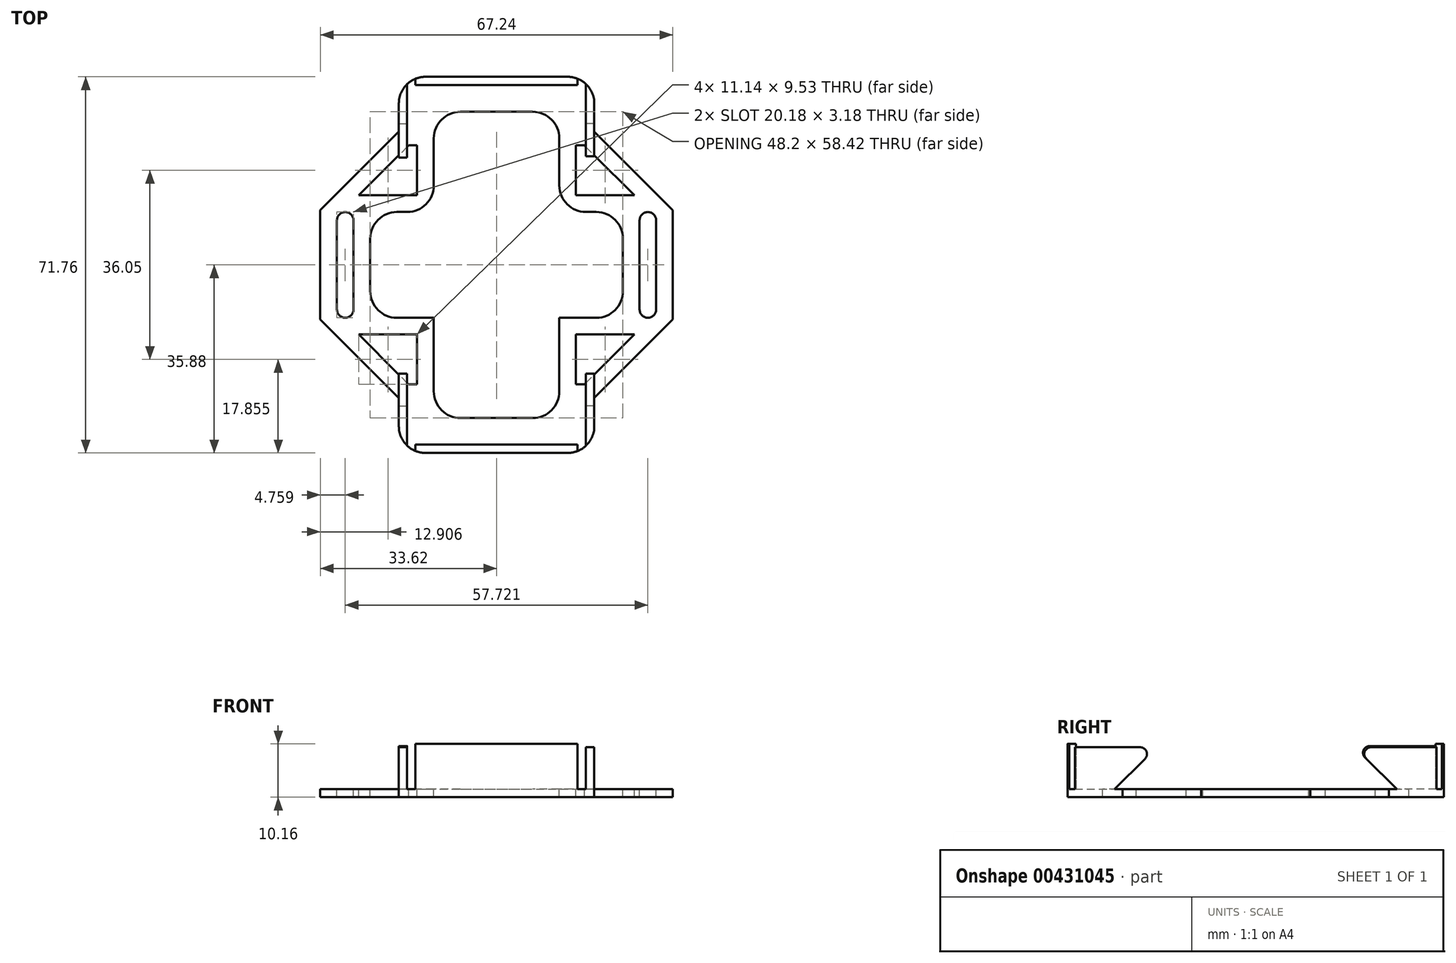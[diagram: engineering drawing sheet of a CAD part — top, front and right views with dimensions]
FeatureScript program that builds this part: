
annotation { "Feature Type Name" : "Feature", "Feature Type Description" : "" }
export const myFeature = defineFeature(function(context is Context, id is Id, definition is map)
    precondition{}
    {
        {
            var Q0;
            Q0=qCreatedBy(makeId("Front.planeOp"),FACE);
            var sketch = newSketch(context, id + "F0", { "sketchPlane" : qUnion([Q0])});
            skLineSegment(sketch, "E0", {"start": v(-17.88, 0.76) * mm, "end": v(17.88, 0.76) * mm});
            skLineSegment(sketch, "E1", {"start": v(17.88, 0.76) * mm, "end": v(18.64, 0) * mm, "construction": true});
            skLineSegment(sketch, "E2", {"start": v(18.64, 0) * mm, "end": v(18.64, -0.76) * mm});
            skLineSegment(sketch, "E3", {"start": v(18.64, -0.76) * mm, "end": v(-18.64, -0.76) * mm});
            skLineSegment(sketch, "E4", {"start": v(-18.64, -0.76) * mm, "end": v(-18.64, 0) * mm});
            skLineSegment(sketch, "E5", {"start": v(-18.64, 0) * mm, "end": v(-17.88, 0.76) * mm, "construction": true});
            skLineSegment(sketch, "E6", {"start": v(0, -0.76) * mm, "end": v(0, 0) * mm, "construction": true});
            skLineSegment(sketch, "E7", {"start": v(0, 0) * mm, "end": v(0, 0.76) * mm, "construction": true});
            skLineSegment(sketch, "E8", {"start": v(18.64, 0) * mm, "end": v(18.64, 0.76) * mm});
            skLineSegment(sketch, "E9", {"start": v(18.64, 0.76) * mm, "end": v(17.88, 0.76) * mm});
            skLineSegment(sketch, "E10", {"start": v(-18.64, 0) * mm, "end": v(-18.64, 0.76) * mm});
            skLineSegment(sketch, "E11", {"start": v(-18.64, 0.76) * mm, "end": v(-17.88, 0.76) * mm});
            skSolve(sketch);
        }
        {
            var Q0;
            Q0=makeQuery(id+"F0.imprint","IMPRINT",FACE,{"disambiguationData":[TD([[makeQuery(id+"F0.imprint","IMPRINT",EDGE,{"derivedFrom":sQuery(id+"F0.wireOp",EDGE,"E0")}),-1.0]])]});
            extrude(context, id + "F1", {"entities" : qUnion([Q0]), "endBound" : BoundingType.SYMMETRIC, "depth" : 71.75 * mm});
        }
        {
            var Q0;
            Q0=qCreatedBy(makeId("Front.planeOp"),FACE);
            var sketch = newSketch(context, id + "F2", { "sketchPlane" : qUnion([Q0])});
            skLineSegment(sketch, "E12", {"start": v(18.64, 0) * mm, "end": v(20.92, 0.76) * mm, "construction": true});
            skLineSegment(sketch, "E13", {"start": v(20.92, 0.76) * mm, "end": v(33.62, 0.76) * mm});
            skLineSegment(sketch, "E14", {"start": v(33.62, 0.76) * mm, "end": v(33.62, -0.76) * mm});
            skLineSegment(sketch, "E15", {"start": v(33.62, -0.76) * mm, "end": v(18.64, -0.76) * mm});
            skLineSegment(sketch, "E16", {"start": v(18.64, -0.76) * mm, "end": v(18.64, -0.76) * mm});
            skLineSegment(sketch, "E17", {"start": v(0, 0) * mm, "end": v(0, 24.67) * mm, "construction": true});
            skLineSegment(sketch, "E18.MirrorCS", {"start": v(-20.92, 0.76) * mm, "end": v(-33.62, 0.76) * mm});
            skLineSegment(sketch, "E19.MirrorCS", {"start": v(-33.62, 0.76) * mm, "end": v(-33.62, -0.76) * mm});
            skLineSegment(sketch, "E20.MirrorCS", {"start": v(-33.62, -0.76) * mm, "end": v(-18.64, -0.76) * mm});
            skLineSegment(sketch, "E21.MirrorCS", {"start": v(-18.64, -0.76) * mm, "end": v(-18.64, 0) * mm});
            skLineSegment(sketch, "E22.MirrorCS", {"start": v(-18.64, 0) * mm, "end": v(-20.92, 0.76) * mm, "construction": true});
            skLineSegment(sketch, "E23", {"start": v(20.92, 0.76) * mm, "end": v(18.64, 0.76) * mm});
            skLineSegment(sketch, "E24", {"start": v(18.64, 0.76) * mm, "end": v(18.64, -0.76) * mm});
            skLineSegment(sketch, "E25", {"start": v(-20.92, 0.76) * mm, "end": v(-18.64, 0.76) * mm});
            skLineSegment(sketch, "E26", {"start": v(-18.64, 0.76) * mm, "end": v(-18.64, 0) * mm});
            skSolve(sketch);
        }
        {
            var Q0;
            Q0 = qSketchRegion(id + "F2", true);
            extrude(context, id + "F3", {"entities" : qUnion([Q0]), "operationType" : NewBodyOperationType.ADD, "endBound" : BoundingType.SYMMETRIC, "depth" : 50.8 * mm});
        }
        {
            var Q0;
            Q0=makeQuery(id+"F3.boolean.opBoolean","MERGE",FACE,{"derivedFrom":[makeQuery(id+"F1.opExtrude","SWEPT_FACE",FACE,{"disambiguationData":[OSD([sQuery(id+"F0.wireOp",EDGE,"E3")])]}),makeQuery(id+"F3.opExtrude","SWEPT_FACE",FACE,{"disambiguationData":[OSD([sQuery(id+"F2.wireOp",EDGE,"E15")])]}),makeQuery(id+"F3.opExtrude","SWEPT_FACE",FACE,{"disambiguationData":[OSD([sQuery(id+"F2.wireOp",EDGE,"E20.MirrorCS")])]})]});
            var sketch = newSketch(context, id + "F4", { "sketchPlane" : qUnion([Q0])});
            skLineSegment(sketch, "E27.bottom", {"start": v(-18.64, 35.88) * mm, "end": v(-17.05, 35.88) * mm});
            skLineSegment(sketch, "E27.top", {"start": v(-18.64, 26.92) * mm, "end": v(-17.05, 26.92) * mm});
            skLineSegment(sketch, "E27.left", {"start": v(-18.64, 35.88) * mm, "end": v(-18.64, 26.92) * mm});
            skLineSegment(sketch, "E27.right", {"start": v(-17.05, 35.88) * mm, "end": v(-17.05, 26.92) * mm});
            skLineSegment(sketch, "E28", {"start": v(0, 0) * mm, "end": v(0, 50.03) * mm, "construction": true});
            skLineSegment(sketch, "E29", {"start": v(30.37, 0) * mm, "end": v(0, 0) * mm, "construction": true});
            skLineSegment(sketch, "E30.MirrorCS", {"start": v(17.05, 35.88) * mm, "end": v(17.05, 26.92) * mm});
            skLineSegment(sketch, "E31.MirrorCS", {"start": v(18.64, 35.88) * mm, "end": v(17.05, 35.88) * mm});
            skLineSegment(sketch, "E32.MirrorCS", {"start": v(18.64, 26.92) * mm, "end": v(17.05, 26.92) * mm});
            skLineSegment(sketch, "E33.MirrorCS", {"start": v(18.64, 35.88) * mm, "end": v(18.64, 26.92) * mm});
            skLineSegment(sketch, "E34.MirrorCS", {"start": v(-17.05, -35.88) * mm, "end": v(-17.05, -26.92) * mm});
            skLineSegment(sketch, "E35.MirrorCS", {"start": v(18.64, -26.92) * mm, "end": v(17.05, -26.92) * mm});
            skLineSegment(sketch, "E36.MirrorCS", {"start": v(-18.64, -35.88) * mm, "end": v(-18.64, -26.92) * mm});
            skLineSegment(sketch, "E37.MirrorCS", {"start": v(17.05, -35.88) * mm, "end": v(17.05, -26.92) * mm});
            skLineSegment(sketch, "E38.MirrorCS", {"start": v(-18.64, -26.92) * mm, "end": v(-17.05, -26.92) * mm});
            skLineSegment(sketch, "E39.MirrorCS", {"start": v(18.64, -35.88) * mm, "end": v(17.05, -35.88) * mm});
            skLineSegment(sketch, "E40.MirrorCS", {"start": v(-18.64, -35.88) * mm, "end": v(-17.05, -35.88) * mm});
            skLineSegment(sketch, "E41.MirrorCS", {"start": v(18.64, -35.88) * mm, "end": v(18.64, -26.92) * mm});
            skSolve(sketch);
        }
        {
            var Q0;
            Q0 = qSketchRegion(id + "F4", true);
            extrude(context, id + "F5", {"entities" : qUnion([Q0]), "operationType" : NewBodyOperationType.ADD, "oppositeDirection" : true, "depth" : 9.52 * mm});
        }
        {
            var Q0;
            Q0=makeQuery(id+"F1.opExtrude","SWEPT_FACE",FACE,{"disambiguationData":[OSD([sQuery(id+"F0.wireOp",EDGE,"E0")])]});
            var sketch = newSketch(context, id + "F6", { "sketchPlane" : qUnion([Q0])});
            skLineSegment(sketch, "E42.bottom", {"start": v(-15.46, 35.88) * mm, "end": v(15.46, 35.88) * mm});
            skLineSegment(sketch, "E42.top", {"start": v(-15.46, 34.3) * mm, "end": v(15.46, 34.3) * mm});
            skLineSegment(sketch, "E42.left", {"start": v(-15.46, 35.88) * mm, "end": v(-15.46, 34.3) * mm});
            skLineSegment(sketch, "E42.right", {"start": v(15.46, 35.88) * mm, "end": v(15.46, 34.3) * mm});
            skLineSegment(sketch, "E43", {"start": v(0, 0) * mm, "end": v(9.45, 0) * mm, "construction": true});
            skLineSegment(sketch, "E44.MirrorCS", {"start": v(-15.46, -35.88) * mm, "end": v(15.46, -35.88) * mm});
            skLineSegment(sketch, "E45.MirrorCS", {"start": v(-15.46, -34.3) * mm, "end": v(15.46, -34.3) * mm});
            skLineSegment(sketch, "E46.MirrorCS", {"start": v(-15.46, -35.88) * mm, "end": v(-15.46, -34.3) * mm});
            skLineSegment(sketch, "E47.MirrorCS", {"start": v(15.46, -35.88) * mm, "end": v(15.46, -34.3) * mm});
            skSolve(sketch);
        }
        {
            var Q0;
            Q0 = qSketchRegion(id + "F6", true);
            var Q1;
            Q1=makeQuery(id+"F5.opExtrude","CAP_FACE",FACE,{"disambiguationData":[OSD([sQuery(id+"F4.wireOp",EDGE,"E34.MirrorCS"),sQuery(id+"F4.wireOp",EDGE,"E36.MirrorCS"),sQuery(id+"F4.wireOp",EDGE,"E38.MirrorCS"),sQuery(id+"F4.wireOp",EDGE,"E40.MirrorCS")])],"isStart":false});
            extrude(context, id + "F7", {"entities" : qUnion([Q0, Q1]), "operationType" : NewBodyOperationType.ADD, "depth" : 8.64 * mm});
        }
        {
            var Q0;
            {var subQ0=sQuery(id+"F4.wireOp",EDGE,"E40.MirrorCS");Q0=makeQuery(id+"F7.boolean.opBoolean","MERGE",FACE,{"derivedFrom":[makeQuery(id+"F5.boolean.opBoolean","MERGE",FACE,{"derivedFrom":[makeQuery(id+"F1.opExtrude","CAP_FACE",FACE,{"disambiguationData":[OSD([sQuery(id+"F0.wireOp",EDGE,"E0"),sQuery(id+"F0.wireOp",EDGE,"E1"),sQuery(id+"F0.wireOp",EDGE,"E2"),sQuery(id+"F0.wireOp",EDGE,"E3"),sQuery(id+"F0.wireOp",EDGE,"E4"),sQuery(id+"F0.wireOp",EDGE,"E5")])],"isStart":true}),makeQuery(id+"F5.opExtrude","SWEPT_FACE",FACE,{"disambiguationData":[OSD([sQuery(id+"F4.wireOp",EDGE,"E39.MirrorCS")])]}),makeQuery(id+"F5.opExtrude","SWEPT_FACE",FACE,{"disambiguationData":[OSD([subQ0])]})]}),makeQuery(id+"F7.opExtrude","SWEPT_FACE",FACE,{"disambiguationData":[OSD([subQ0])]}),makeQuery(id+"F7.opExtrude","SWEPT_FACE",FACE,{"disambiguationData":[OSD([sQuery(id+"F6.wireOp",EDGE,"E42.bottom")])]})]});}
            var sketch = newSketch(context, id + "F8", { "sketchPlane" : qUnion([Q0])});
            skLineSegment(sketch, "E48.bottom", {"start": v(16.08, 16.65) * mm, "end": v(21.03, 16.65) * mm});
            skLineSegment(sketch, "E48.top", {"start": v(16.08, 9) * mm, "end": v(21.03, 9) * mm});
            skLineSegment(sketch, "E48.left", {"start": v(16.08, 16.65) * mm, "end": v(16.08, 9) * mm});
            skLineSegment(sketch, "E48.right", {"start": v(21.03, 16.65) * mm, "end": v(21.03, 9) * mm});
            skSolve(sketch);
        }
        {
            var Q0;
            Q0 = qSketchRegion(id + "F8", true);
            extrude(context, id + "F9", {"entities" : qUnion([Q0]), "operationType" : NewBodyOperationType.REMOVE, "endBound" : BoundingType.THROUGH_ALL, "oppositeDirection" : true, "depth" : 25.4 * mm});
        }
        {
            var Q0;
            Q0=makeQuery(id+"F3.opExtrude","SWEPT_FACE",FACE,{"disambiguationData":[OSD([sQuery(id+"F2.wireOp",EDGE,"E18.MirrorCS")])]});
            var sketch = newSketch(context, id + "F10", { "sketchPlane" : qUnion([Q0])});
            skLineSegment(sketch, "E49", {"start": v(-28.86, -8.5) * mm, "end": v(-28.86, 8.5) * mm});
            skLineSegment(sketch, "E50", {"start": v(-28.86, 8.5) * mm, "end": v(-28.86, 25.4) * mm, "construction": true});
            skLineSegment(sketch, "E51", {"start": v(-28.86, -25.4) * mm, "end": v(-28.86, -8.5) * mm, "construction": true});
            skArc(sketch, "E52.0.startCap", {"start": v(-27.27, -8.5) * mm, "mid": v(-28.86, -10.09) * mm, "end": v(-30.45, -8.5) * mm});
            skArc(sketch, "E52.0.endCap", {"start": v(-30.45, 8.5) * mm, "mid": v(-28.86, 10.09) * mm, "end": v(-27.27, 8.5) * mm});
            skLineSegment(sketch, "E52.0.left", {"start": v(-30.45, -8.5) * mm, "end": v(-30.45, 8.5) * mm});
            skLineSegment(sketch, "E52.0.right", {"start": v(-27.27, -8.5) * mm, "end": v(-27.27, 8.5) * mm});
            skLineSegment(sketch, "E53", {"start": v(0, 0) * mm, "end": v(0, 13.67) * mm, "construction": true});
            skArc(sketch, "E54.MirrorCS", {"start": v(27.27, -8.5) * mm, "mid": v(28.86, -10.09) * mm, "end": v(30.45, -8.5) * mm});
            skArc(sketch, "E55.MirrorCS", {"start": v(30.45, 8.5) * mm, "mid": v(28.86, 10.09) * mm, "end": v(27.27, 8.5) * mm});
            skLineSegment(sketch, "E56.MirrorCS", {"start": v(30.45, -8.5) * mm, "end": v(30.45, 8.5) * mm});
            skLineSegment(sketch, "E57.MirrorCS", {"start": v(27.27, -8.5) * mm, "end": v(27.27, 8.5) * mm});
            skLineSegment(sketch, "E58.bottom", {"start": v(-11.97, 29.21) * mm, "end": v(11.97, 29.21) * mm});
            skLineSegment(sketch, "E58.top", {"start": v(-11.97, -29.21) * mm, "end": v(11.97, -29.21) * mm});
            skLineSegment(sketch, "E58.left", {"start": v(-11.97, 29.21) * mm, "end": v(-11.97, -29.21) * mm});
            skLineSegment(sketch, "E58.right", {"start": v(11.97, 29.21) * mm, "end": v(11.97, -29.21) * mm});
            skSolve(sketch);
        }
        {
            var Q0;
            Q0 = qSketchRegion(id + "F10", true);
            extrude(context, id + "F11", {"entities" : qUnion([Q0]), "operationType" : NewBodyOperationType.REMOVE, "endBound" : BoundingType.THROUGH_ALL, "oppositeDirection" : true, "depth" : 25.4 * mm});
        }
        {
            var Q0;
            Q0=makeQuery(id+"F3.boolean.opBoolean","MERGE",FACE,{"derivedFrom":[makeQuery(id+"F1.opExtrude","SWEPT_FACE",FACE,{"disambiguationData":[OSD([sQuery(id+"F0.wireOp",EDGE,"E0"),sQuery(id+"F0.wireOp",EDGE,"E9"),sQuery(id+"F0.wireOp",EDGE,"E11")])]}),makeQuery(id+"F3.opExtrude","SWEPT_FACE",FACE,{"disambiguationData":[OSD([sQuery(id+"F2.wireOp",EDGE,"E13"),sQuery(id+"F2.wireOp",EDGE,"E23")])]}),makeQuery(id+"F3.opExtrude","SWEPT_FACE",FACE,{"disambiguationData":[OSD([sQuery(id+"F2.wireOp",EDGE,"E18.MirrorCS"),sQuery(id+"F2.wireOp",EDGE,"E25")])]})]});
            var sketch = newSketch(context, id + "F12", { "sketchPlane" : qUnion([Q0])});
            skLineSegment(sketch, "E59", {"start": v(18.64, 25.4) * mm, "end": v(33.62, 10.41) * mm});
            skLineSegment(sketch, "E60", {"start": v(33.62, 10.41) * mm, "end": v(33.62, 25.4) * mm});
            skLineSegment(sketch, "E61", {"start": v(33.62, 25.4) * mm, "end": v(18.64, 25.4) * mm});
            skLineSegment(sketch, "E62", {"start": v(18.64, -25.4) * mm, "end": v(33.62, -10.41) * mm});
            skLineSegment(sketch, "E63", {"start": v(33.62, -10.41) * mm, "end": v(33.62, -25.4) * mm});
            skLineSegment(sketch, "E64", {"start": v(33.62, -25.4) * mm, "end": v(18.64, -25.4) * mm});
            skLineSegment(sketch, "E65", {"start": v(-33.62, 25.4) * mm, "end": v(-18.64, 25.4) * mm});
            skLineSegment(sketch, "E66", {"start": v(-18.64, 25.4) * mm, "end": v(-33.62, 10.41) * mm});
            skLineSegment(sketch, "E67", {"start": v(-33.62, 10.41) * mm, "end": v(-33.62, 25.4) * mm});
            skLineSegment(sketch, "E68", {"start": v(-33.62, -25.4) * mm, "end": v(-18.64, -25.4) * mm});
            skLineSegment(sketch, "E69", {"start": v(-18.64, -25.4) * mm, "end": v(-33.62, -10.41) * mm});
            skLineSegment(sketch, "E70", {"start": v(-33.62, -10.41) * mm, "end": v(-33.62, -25.4) * mm});
            skSolve(sketch);
        }
        {
            var Q0;
            Q0 = qSketchRegion(id + "F12", true);
            extrude(context, id + "F13", {"entities" : qUnion([Q0]), "operationType" : NewBodyOperationType.REMOVE, "oppositeDirection" : true, "depth" : 25.4 * mm});
        }
        {
            var Q0;
            Q0=makeQuery(id+"F3.boolean.opBoolean","MERGE",FACE,{"derivedFrom":[makeQuery(id+"F1.opExtrude","SWEPT_FACE",FACE,{"disambiguationData":[OSD([sQuery(id+"F0.wireOp",EDGE,"E0"),sQuery(id+"F0.wireOp",EDGE,"E9"),sQuery(id+"F0.wireOp",EDGE,"E11")])]}),makeQuery(id+"F3.opExtrude","SWEPT_FACE",FACE,{"disambiguationData":[OSD([sQuery(id+"F2.wireOp",EDGE,"E13"),sQuery(id+"F2.wireOp",EDGE,"E23")])]}),makeQuery(id+"F3.opExtrude","SWEPT_FACE",FACE,{"disambiguationData":[OSD([sQuery(id+"F2.wireOp",EDGE,"E18.MirrorCS"),sQuery(id+"F2.wireOp",EDGE,"E25")])]})]});
            var sketch = newSketch(context, id + "F14", { "sketchPlane" : qUnion([Q0])});
            skLineSegment(sketch, "E71", {"start": v(-11.97, 10.09) * mm, "end": v(-24.1, 10.09) * mm});
            skLineSegment(sketch, "E72", {"start": v(-24.1, 10.09) * mm, "end": v(-24.1, -10.09) * mm});
            skLineSegment(sketch, "E73", {"start": v(-24.1, -10.09) * mm, "end": v(-11.97, -10.09) * mm});
            skLineSegment(sketch, "E74", {"start": v(-11.97, -10.09) * mm, "end": v(-11.97, 10.09) * mm});
            skLineSegment(sketch, "E75", {"start": v(-28.86, 10.09) * mm, "end": v(-24.1, 10.09) * mm, "construction": true});
            skLineSegment(sketch, "E76", {"start": v(-28.86, -10.09) * mm, "end": v(-24.1, -10.09) * mm, "construction": true});
            skLineSegment(sketch, "E77", {"start": v(-33.62, 0) * mm, "end": v(-30.45, 0) * mm, "construction": true});
            skLineSegment(sketch, "E78", {"start": v(-27.27, 0) * mm, "end": v(-24.1, 0) * mm, "construction": true});
            skLineSegment(sketch, "E79", {"start": v(0, 0) * mm, "end": v(0, -13.97) * mm, "construction": true});
            skLineSegment(sketch, "E80.MirrorCS", {"start": v(24.1, -10.09) * mm, "end": v(11.97, -10.09) * mm});
            skLineSegment(sketch, "E81.MirrorCS", {"start": v(11.97, -10.09) * mm, "end": v(11.97, 10.09) * mm});
            skLineSegment(sketch, "E82.MirrorCS", {"start": v(11.97, 10.09) * mm, "end": v(24.1, 10.09) * mm});
            skLineSegment(sketch, "E83.MirrorCS", {"start": v(24.1, 10.09) * mm, "end": v(24.1, -10.09) * mm});
            skLineSegment(sketch, "E84", {"start": v(-23.1, 16.44) * mm, "end": v(-26.28, 13.26) * mm});
            skLineSegment(sketch, "E85", {"start": v(-26.28, 13.26) * mm, "end": v(-15.14, 13.26) * mm});
            skLineSegment(sketch, "E86", {"start": v(-15.14, 13.26) * mm, "end": v(-15.14, 16.44) * mm});
            skLineSegment(sketch, "E87", {"start": v(-15.14, 16.44) * mm, "end": v(-23.1, 16.44) * mm});
            skLineSegment(sketch, "E88", {"start": v(-18.03, 13.26) * mm, "end": v(-18.03, 10.09) * mm, "construction": true});
            skLineSegment(sketch, "E89", {"start": v(-15.14, 16.36) * mm, "end": v(-11.97, 16.36) * mm, "construction": true});
            skLineSegment(sketch, "E90", {"start": v(-26.94, 17.1) * mm, "end": v(-24.7, 14.85) * mm, "construction": true});
            skLineSegment(sketch, "E91", {"start": v(-16.76, 19.61) * mm, "end": v(-15.14, 19.61) * mm});
            skLineSegment(sketch, "E92", {"start": v(-15.14, 19.61) * mm, "end": v(-15.14, 22.79) * mm});
            skLineSegment(sketch, "E93", {"start": v(-15.14, 22.79) * mm, "end": v(-16.76, 22.79) * mm});
            skLineSegment(sketch, "E94", {"start": v(-16.76, 22.79) * mm, "end": v(-16.76, 19.61) * mm, "construction": true});
            skLineSegment(sketch, "E95", {"start": v(-15.95, 19.61) * mm, "end": v(-15.95, 16.44) * mm, "construction": true});
            skLineSegment(sketch, "E96", {"start": v(-16.76, 22.79) * mm, "end": v(-19, 25.03) * mm, "construction": true});
            skLineSegment(sketch, "E97", {"start": v(-16.76, 22.79) * mm, "end": v(-19.93, 19.61) * mm});
            skLineSegment(sketch, "E98", {"start": v(-19.93, 19.61) * mm, "end": v(-16.76, 19.61) * mm});
            skLineSegment(sketch, "E99.MirrorCS", {"start": v(19.93, 19.61) * mm, "end": v(16.76, 19.61) * mm});
            skLineSegment(sketch, "E100.MirrorCS", {"start": v(15.14, 22.79) * mm, "end": v(16.76, 22.79) * mm});
            skLineSegment(sketch, "E101.MirrorCS", {"start": v(15.14, 16.44) * mm, "end": v(23.1, 16.44) * mm});
            skLineSegment(sketch, "E102.MirrorCS", {"start": v(23.1, 16.44) * mm, "end": v(26.28, 13.26) * mm});
            skLineSegment(sketch, "E103.MirrorCS", {"start": v(16.76, 19.61) * mm, "end": v(15.14, 19.61) * mm});
            skLineSegment(sketch, "E104.MirrorCS", {"start": v(15.14, 13.26) * mm, "end": v(15.14, 16.44) * mm});
            skLineSegment(sketch, "E105.MirrorCS", {"start": v(15.14, 19.61) * mm, "end": v(15.14, 22.79) * mm});
            skLineSegment(sketch, "E106.MirrorCS", {"start": v(16.76, 22.79) * mm, "end": v(19.93, 19.61) * mm});
            skLineSegment(sketch, "E107", {"start": v(15.14, 13.26) * mm, "end": v(26.28, 13.26) * mm});
            skLineSegment(sketch, "E108", {"start": v(0, 0) * mm, "end": v(6.74, 0) * mm, "construction": true});
            skLineSegment(sketch, "E109.MirrorCS", {"start": v(15.14, -13.26) * mm, "end": v(26.28, -13.26) * mm});
            skLineSegment(sketch, "E110.MirrorCS", {"start": v(15.14, -13.26) * mm, "end": v(15.14, -16.44) * mm});
            skLineSegment(sketch, "E111.MirrorCS", {"start": v(15.14, -16.44) * mm, "end": v(23.1, -16.44) * mm});
            skLineSegment(sketch, "E112.MirrorCS", {"start": v(23.1, -16.44) * mm, "end": v(26.28, -13.26) * mm});
            skLineSegment(sketch, "E113.MirrorCS", {"start": v(19.93, -19.61) * mm, "end": v(16.76, -19.61) * mm});
            skLineSegment(sketch, "E114.MirrorCS", {"start": v(16.76, -22.79) * mm, "end": v(19.93, -19.61) * mm});
            skLineSegment(sketch, "E115.MirrorCS", {"start": v(16.76, -19.61) * mm, "end": v(15.14, -19.61) * mm});
            skLineSegment(sketch, "E116.MirrorCS", {"start": v(15.14, -19.61) * mm, "end": v(15.14, -22.79) * mm});
            skLineSegment(sketch, "E117.MirrorCS", {"start": v(15.14, -22.79) * mm, "end": v(16.76, -22.79) * mm});
            skLineSegment(sketch, "E118.MirrorCS", {"start": v(-26.28, -13.26) * mm, "end": v(-15.14, -13.26) * mm});
            skLineSegment(sketch, "E119.MirrorCS", {"start": v(-23.1, -16.44) * mm, "end": v(-26.28, -13.26) * mm});
            skLineSegment(sketch, "E120.MirrorCS", {"start": v(-15.14, -16.44) * mm, "end": v(-23.1, -16.44) * mm});
            skLineSegment(sketch, "E121.MirrorCS", {"start": v(-15.14, -13.26) * mm, "end": v(-15.14, -16.44) * mm});
            skLineSegment(sketch, "E122.MirrorCS", {"start": v(-16.76, -19.61) * mm, "end": v(-15.14, -19.61) * mm});
            skLineSegment(sketch, "E123.MirrorCS", {"start": v(-19.93, -19.61) * mm, "end": v(-16.76, -19.61) * mm});
            skLineSegment(sketch, "E124.MirrorCS", {"start": v(-16.76, -22.79) * mm, "end": v(-19.93, -19.61) * mm});
            skLineSegment(sketch, "E125.MirrorCS", {"start": v(-15.14, -19.61) * mm, "end": v(-15.14, -22.79) * mm});
            skLineSegment(sketch, "E126.MirrorCS", {"start": v(-15.14, -22.79) * mm, "end": v(-16.76, -22.79) * mm});
            skSolve(sketch);
        }
        {
            var Q0;
            Q0 = qSketchRegion(id + "F14", true);
            extrude(context, id + "F15", {"entities" : qUnion([Q0]), "operationType" : NewBodyOperationType.REMOVE, "oppositeDirection" : true, "depth" : 25.4 * mm});
        }
        {
            var Q0;
            Q0=makeQuery(id+"F13.boolean.opBoolean","COPY",EDGE,{"derivedFrom":makeQuery(id+"F13.opExtrude","SWEPT_EDGE",EDGE,{"disambiguationData":[OSD([sQuery(id+"F2.wireOp",EDGE,"E18.MirrorCS"),sQuery(id+"F2.wireOp",EDGE,"E19.MirrorCS"),sQuery(id+"F12.wireOp",EDGE,"E69"),sQuery(id+"F12.wireOp",EDGE,"E70")])]})});
            var Q1;
            Q1=makeQuery(id+"F13.boolean.opBoolean","COPY",EDGE,{"derivedFrom":makeQuery(id+"F13.opExtrude","SWEPT_EDGE",EDGE,{"disambiguationData":[OSD([sQuery(id+"F2.wireOp",EDGE,"E18.MirrorCS"),sQuery(id+"F2.wireOp",EDGE,"E19.MirrorCS"),sQuery(id+"F12.wireOp",EDGE,"E66"),sQuery(id+"F12.wireOp",EDGE,"E67")])]})});
            var Q2;
            Q2=makeQuery(id+"F15.boolean.opBoolean","COPY",EDGE,{"derivedFrom":makeQuery(id+"F15.opExtrude","SWEPT_EDGE",EDGE,{"disambiguationData":[OSD([sQuery(id+"F14.wireOp",EDGE,"E71"),sQuery(id+"F14.wireOp",EDGE,"E72")])]})});
            var Q3;
            Q3=makeQuery(id+"F15.boolean.opBoolean","COPY",EDGE,{"derivedFrom":makeQuery(id+"F15.opExtrude","SWEPT_EDGE",EDGE,{"disambiguationData":[OSD([sQuery(id+"F14.wireOp",EDGE,"E72"),sQuery(id+"F14.wireOp",EDGE,"E73")])]})});
            var Q4;
            Q4=makeQuery(id+"F15.boolean.opBoolean","COPY",EDGE,{"derivedFrom":makeQuery(id+"F15.opExtrude","SWEPT_EDGE",EDGE,{"disambiguationData":[OSD([sQuery(id+"F10.wireOp",EDGE,"E58.left"),sQuery(id+"F14.wireOp",EDGE,"E73"),sQuery(id+"F14.wireOp",EDGE,"E74")])]})});
            var Q5;
            Q5=makeQuery(id+"F15.boolean.opBoolean","COPY",EDGE,{"derivedFrom":makeQuery(id+"F15.opExtrude","SWEPT_EDGE",EDGE,{"disambiguationData":[OSD([sQuery(id+"F10.wireOp",EDGE,"E58.left"),sQuery(id+"F14.wireOp",EDGE,"E71"),sQuery(id+"F14.wireOp",EDGE,"E74")])]})});
            var Q6;
            Q6=makeQuery(id+"F11.boolean.opBoolean","COPY",EDGE,{"derivedFrom":makeQuery(id+"F11.opExtrude","SWEPT_EDGE",EDGE,{"disambiguationData":[OSD([sQuery(id+"F10.wireOp",EDGE,"E58.bottom"),sQuery(id+"F10.wireOp",EDGE,"E58.left")])]})});
            var Q7;
            Q7=makeQuery(id+"F11.boolean.opBoolean","COPY",EDGE,{"derivedFrom":makeQuery(id+"F11.opExtrude","SWEPT_EDGE",EDGE,{"disambiguationData":[OSD([sQuery(id+"F10.wireOp",EDGE,"E58.bottom"),sQuery(id+"F10.wireOp",EDGE,"E58.right")])]})});
            var Q8;
            Q8=makeQuery(id+"F15.boolean.opBoolean","COPY",EDGE,{"derivedFrom":makeQuery(id+"F15.opExtrude","SWEPT_EDGE",EDGE,{"disambiguationData":[OSD([sQuery(id+"F10.wireOp",EDGE,"E58.right"),sQuery(id+"F14.wireOp",EDGE,"E81.MirrorCS"),sQuery(id+"F14.wireOp",EDGE,"E82.MirrorCS")])]})});
            var Q9;
            Q9=makeQuery(id+"F15.boolean.opBoolean","COPY",EDGE,{"derivedFrom":makeQuery(id+"F15.opExtrude","SWEPT_EDGE",EDGE,{"disambiguationData":[OSD([sQuery(id+"F14.wireOp",EDGE,"E82.MirrorCS"),sQuery(id+"F14.wireOp",EDGE,"E83.MirrorCS")])]})});
            var Q10;
            Q10=makeQuery(id+"F15.boolean.opBoolean","COPY",EDGE,{"derivedFrom":makeQuery(id+"F15.opExtrude","SWEPT_EDGE",EDGE,{"disambiguationData":[OSD([sQuery(id+"F14.wireOp",EDGE,"E80.MirrorCS"),sQuery(id+"F14.wireOp",EDGE,"E83.MirrorCS")])]})});
            var Q11;
            Q11=makeQuery(id+"F15.boolean.opBoolean","COPY",EDGE,{"derivedFrom":makeQuery(id+"F15.opExtrude","SWEPT_EDGE",EDGE,{"disambiguationData":[OSD([sQuery(id+"F10.wireOp",EDGE,"E58.right"),sQuery(id+"F14.wireOp",EDGE,"E80.MirrorCS"),sQuery(id+"F14.wireOp",EDGE,"E81.MirrorCS")])]})});
            var Q12;
            Q12=makeQuery(id+"F11.boolean.opBoolean","COPY",EDGE,{"derivedFrom":makeQuery(id+"F11.opExtrude","SWEPT_EDGE",EDGE,{"disambiguationData":[OSD([sQuery(id+"F10.wireOp",EDGE,"E58.top"),sQuery(id+"F10.wireOp",EDGE,"E58.right")])]})});
            var Q13;
            Q13=makeQuery(id+"F11.boolean.opBoolean","COPY",EDGE,{"derivedFrom":makeQuery(id+"F11.opExtrude","SWEPT_EDGE",EDGE,{"disambiguationData":[OSD([sQuery(id+"F10.wireOp",EDGE,"E58.top"),sQuery(id+"F10.wireOp",EDGE,"E58.left")])]})});
            var Q14;
            Q14=makeQuery(id+"F13.boolean.opBoolean","COPY",EDGE,{"derivedFrom":makeQuery(id+"F13.opExtrude","SWEPT_EDGE",EDGE,{"disambiguationData":[OSD([sQuery(id+"F2.wireOp",EDGE,"E13"),sQuery(id+"F2.wireOp",EDGE,"E14"),sQuery(id+"F12.wireOp",EDGE,"E62"),sQuery(id+"F12.wireOp",EDGE,"E63")])]})});
            var Q15;
            Q15=makeQuery(id+"F13.boolean.opBoolean","COPY",EDGE,{"derivedFrom":makeQuery(id+"F13.opExtrude","SWEPT_EDGE",EDGE,{"disambiguationData":[OSD([sQuery(id+"F2.wireOp",EDGE,"E13"),sQuery(id+"F2.wireOp",EDGE,"E14"),sQuery(id+"F12.wireOp",EDGE,"E59"),sQuery(id+"F12.wireOp",EDGE,"E60")])]})});
            var Q16;
            Q16=makeQuery(id+"F5.boolean.opBoolean","MERGE",EDGE,{"derivedFrom":[makeQuery(id+"F1.opExtrude","CAP_EDGE",EDGE,{"disambiguationData":[OSD([sQuery(id+"F0.wireOp",EDGE,"E2"),sQuery(id+"F0.wireOp",EDGE,"E8")])],"isStart":true}),makeQuery(id+"F5.opExtrude","SWEPT_EDGE",EDGE,{"disambiguationData":[OSD([sQuery(id+"F4.wireOp",EDGE,"E39.MirrorCS"),sQuery(id+"F4.wireOp",EDGE,"E41.MirrorCS")])]})]});
            var Q17;
            {var subQ0=sQuery(id+"F4.wireOp",EDGE,"E40.MirrorCS");var subQ1=sQuery(id+"F4.wireOp",EDGE,"E36.MirrorCS");Q17=makeQuery(id+"F7.boolean.opBoolean","MERGE",EDGE,{"derivedFrom":[makeQuery(id+"F5.boolean.opBoolean","MERGE",EDGE,{"derivedFrom":[makeQuery(id+"F1.opExtrude","CAP_EDGE",EDGE,{"disambiguationData":[OSD([sQuery(id+"F0.wireOp",EDGE,"E4"),sQuery(id+"F0.wireOp",EDGE,"E10")])],"isStart":true}),makeQuery(id+"F5.opExtrude","SWEPT_EDGE",EDGE,{"disambiguationData":[OSD([subQ1,subQ0])]})]}),makeQuery(id+"F7.opExtrude","SWEPT_EDGE",EDGE,{"disambiguationData":[OSD([subQ1,subQ0])]})]});}
            var Q18;
            Q18=makeQuery(id+"F5.boolean.opBoolean","MERGE",EDGE,{"derivedFrom":[makeQuery(id+"F1.opExtrude","CAP_EDGE",EDGE,{"disambiguationData":[OSD([sQuery(id+"F0.wireOp",EDGE,"E2"),sQuery(id+"F0.wireOp",EDGE,"E8")])],"isStart":false}),makeQuery(id+"F5.opExtrude","SWEPT_EDGE",EDGE,{"disambiguationData":[OSD([sQuery(id+"F4.wireOp",EDGE,"E31.MirrorCS"),sQuery(id+"F4.wireOp",EDGE,"E33.MirrorCS")])]})]});
            var Q19;
            Q19=makeQuery(id+"F5.boolean.opBoolean","MERGE",EDGE,{"derivedFrom":[makeQuery(id+"F1.opExtrude","CAP_EDGE",EDGE,{"disambiguationData":[OSD([sQuery(id+"F0.wireOp",EDGE,"E4"),sQuery(id+"F0.wireOp",EDGE,"E10")])],"isStart":false}),makeQuery(id+"F5.opExtrude","SWEPT_EDGE",EDGE,{"disambiguationData":[OSD([sQuery(id+"F4.wireOp",EDGE,"E27.bottom"),sQuery(id+"F4.wireOp",EDGE,"E27.left")])]})]});
            fillet(context, id + "F16", {"entities" : qUnion([Q0, Q1, Q2, Q3, Q4, Q5, Q6, Q7, Q8, Q9, Q10, Q11, Q12, Q13, Q14, Q15, Q16, Q17, Q18, Q19]), "radius" : 5.08 * mm, "tangentPropagation" : true, "allowEdgeOverflow" : false});
        }
        {
            var Q0;
            Q0=makeQuery(id+"F3.boolean.opBoolean","MERGE",FACE,{"derivedFrom":[makeQuery(id+"F1.opExtrude","SWEPT_FACE",FACE,{"disambiguationData":[OSD([sQuery(id+"F0.wireOp",EDGE,"E0"),sQuery(id+"F0.wireOp",EDGE,"E9"),sQuery(id+"F0.wireOp",EDGE,"E11")])]}),makeQuery(id+"F3.opExtrude","SWEPT_FACE",FACE,{"disambiguationData":[OSD([sQuery(id+"F2.wireOp",EDGE,"E13"),sQuery(id+"F2.wireOp",EDGE,"E23")])]}),makeQuery(id+"F3.opExtrude","SWEPT_FACE",FACE,{"disambiguationData":[OSD([sQuery(id+"F2.wireOp",EDGE,"E18.MirrorCS"),sQuery(id+"F2.wireOp",EDGE,"E25")])]})]});
            var sketch = newSketch(context, id + "F17", { "sketchPlane" : qUnion([Q0])});
            skLineSegment(sketch, "E127", {"start": v(-19.93, 19.61) * mm, "end": v(-23.1, 16.44) * mm});
            skLineSegment(sketch, "E128", {"start": v(-23.1, 16.44) * mm, "end": v(-15.14, 16.44) * mm});
            skLineSegment(sketch, "E129", {"start": v(-15.14, 16.44) * mm, "end": v(-15.14, 19.61) * mm});
            skLineSegment(sketch, "E130", {"start": v(-15.14, 19.61) * mm, "end": v(-19.93, 19.61) * mm});
            skLineSegment(sketch, "E131", {"start": v(15.14, 19.61) * mm, "end": v(15.14, 16.44) * mm});
            skLineSegment(sketch, "E132", {"start": v(15.14, 16.44) * mm, "end": v(23.1, 16.44) * mm});
            skLineSegment(sketch, "E133", {"start": v(23.1, 16.44) * mm, "end": v(19.93, 19.61) * mm});
            skLineSegment(sketch, "E134", {"start": v(19.93, 19.61) * mm, "end": v(15.14, 19.61) * mm});
            skLineSegment(sketch, "E135", {"start": v(15.14, -16.44) * mm, "end": v(15.14, -19.61) * mm});
            skLineSegment(sketch, "E136", {"start": v(15.14, -19.61) * mm, "end": v(19.93, -19.61) * mm});
            skLineSegment(sketch, "E137", {"start": v(19.93, -19.61) * mm, "end": v(23.1, -16.44) * mm});
            skLineSegment(sketch, "E138", {"start": v(23.1, -16.44) * mm, "end": v(15.14, -16.44) * mm});
            skLineSegment(sketch, "E139", {"start": v(-23.1, -16.44) * mm, "end": v(-19.93, -19.61) * mm});
            skLineSegment(sketch, "E140", {"start": v(-19.93, -19.61) * mm, "end": v(-15.14, -19.61) * mm});
            skLineSegment(sketch, "E141", {"start": v(-15.14, -19.61) * mm, "end": v(-15.14, -16.44) * mm});
            skLineSegment(sketch, "E142", {"start": v(-15.14, -16.44) * mm, "end": v(-23.1, -16.44) * mm});
            skSolve(sketch);
        }
        {
            var Q0;
            Q0 = qSketchRegion(id + "F17", true);
            extrude(context, id + "F18", {"entities" : qUnion([Q0]), "operationType" : NewBodyOperationType.REMOVE, "oppositeDirection" : true, "depth" : 25.4 * mm});
        }
        {
            var Q0;
            {var subQ0=sQuery(id+"F2.wireOp",EDGE,"E23");var subQ1=sQuery(id+"F2.wireOp",EDGE,"E15");var subQ2=sQuery(id+"F2.wireOp",EDGE,"E13");var subQ7=sQuery(id+"F0.wireOp",EDGE,"E8");var subQ8=sQuery(id+"F0.wireOp",EDGE,"E2");Q0=makeQuery(id+"F5.boolean.opBoolean","MERGE",FACE,{"derivedFrom":[makeQuery(id+"F3.boolean.opBoolean","SPLIT",FACE,{"disambiguationData":[TD([makeQuery(id+"F3.opExtrude","CAP_FACE",FACE,{"disambiguationData":[OSD([subQ2,sQuery(id+"F2.wireOp",EDGE,"E14"),subQ1,subQ0,sQuery(id+"F2.wireOp",EDGE,"E24")])],"isStart":true})])],"derivedFrom":makeQuery(id+"F1.opExtrude","SWEPT_FACE",FACE,{"disambiguationData":[OSD([subQ8,subQ7])]})}),makeQuery(id+"F5.opExtrude","SWEPT_FACE",FACE,{"disambiguationData":[OSD([sQuery(id+"F4.wireOp",EDGE,"E41.MirrorCS")])]})]});}
            var sketch = newSketch(context, id + "F19", { "sketchPlane" : qUnion([Q0])});
            skLineSegment(sketch, "E143", {"start": v(26.92, 0.76) * mm, "end": v(18.92, 8.76) * mm});
            skLineSegment(sketch, "E144", {"start": v(18.92, 8.76) * mm, "end": v(26.92, 8.76) * mm});
            skLineSegment(sketch, "E145", {"start": v(26.92, 8.76) * mm, "end": v(26.92, 0.76) * mm});
            skLineSegment(sketch, "E146", {"start": v(0, 0) * mm, "end": v(0, 31.58) * mm, "construction": true});
            skLineSegment(sketch, "E147.MirrorCS", {"start": v(-26.92, 0.76) * mm, "end": v(-18.92, 8.76) * mm});
            skLineSegment(sketch, "E148.MirrorCS", {"start": v(-18.92, 8.76) * mm, "end": v(-26.92, 8.76) * mm});
            skLineSegment(sketch, "E149.MirrorCS", {"start": v(-26.92, 8.76) * mm, "end": v(-26.92, 0.76) * mm});
            skSolve(sketch);
        }
        {
            var Q0;
            Q0 = qSketchRegion(id + "F19", true);
            extrude(context, id + "F20", {"entities" : qUnion([Q0]), "operationType" : NewBodyOperationType.ADD, "oppositeDirection" : true, "depth" : 1.59 * mm});
        }
        {
            var Q0;
            {var subQ4=sQuery(id+"F0.wireOp",EDGE,"E10");var subQ5=sQuery(id+"F0.wireOp",EDGE,"E4");var subQ6=sQuery(id+"F2.wireOp",EDGE,"E25");var subQ7=sQuery(id+"F2.wireOp",EDGE,"E20.MirrorCS");var subQ8=sQuery(id+"F2.wireOp",EDGE,"E18.MirrorCS");Q0=makeQuery(id+"F5.boolean.opBoolean","MERGE",FACE,{"derivedFrom":[makeQuery(id+"F3.boolean.opBoolean","SPLIT",FACE,{"disambiguationData":[TD([makeQuery(id+"F3.opExtrude","CAP_FACE",FACE,{"disambiguationData":[OSD([subQ8,sQuery(id+"F2.wireOp",EDGE,"E19.MirrorCS"),subQ7,sQuery(id+"F2.wireOp",EDGE,"E21.MirrorCS"),subQ6,sQuery(id+"F2.wireOp",EDGE,"E26")])],"isStart":false})])],"derivedFrom":makeQuery(id+"F1.opExtrude","SWEPT_FACE",FACE,{"disambiguationData":[OSD([subQ5,subQ4])]})}),makeQuery(id+"F5.opExtrude","SWEPT_FACE",FACE,{"disambiguationData":[OSD([sQuery(id+"F4.wireOp",EDGE,"E27.left")])]})]});}
            var sketch = newSketch(context, id + "F21", { "sketchPlane" : qUnion([Q0])});
            skLineSegment(sketch, "E150", {"start": v(26.92, 0.76) * mm, "end": v(18.92, 8.76) * mm});
            skLineSegment(sketch, "E151", {"start": v(18.92, 8.76) * mm, "end": v(26.92, 8.76) * mm});
            skLineSegment(sketch, "E152", {"start": v(26.92, 8.76) * mm, "end": v(26.92, 0.76) * mm});
            skLineSegment(sketch, "E153", {"start": v(-26.92, 0.76) * mm, "end": v(-26.92, 9) * mm});
            skLineSegment(sketch, "E154", {"start": v(-26.92, 9) * mm, "end": v(-18.69, 9) * mm});
            skLineSegment(sketch, "E155", {"start": v(-18.69, 9) * mm, "end": v(-26.92, 0.76) * mm});
            skSolve(sketch);
        }
        {
            var Q0;
            Q0 = qSketchRegion(id + "F21", true);
            extrude(context, id + "F22", {"entities" : qUnion([Q0]), "operationType" : NewBodyOperationType.ADD, "oppositeDirection" : true, "depth" : 1.59 * mm});
        }
        {
            var Q0;
            Q0=makeQuery(id+"F22.opExtrude","SWEPT_EDGE",EDGE,{"disambiguationData":[OSD([sQuery(id+"F21.wireOp",EDGE,"E154"),sQuery(id+"F21.wireOp",EDGE,"E155")])]});
            var Q1;
            Q1=makeQuery(id+"F22.opExtrude","SWEPT_EDGE",EDGE,{"disambiguationData":[OSD([sQuery(id+"F21.wireOp",EDGE,"E150"),sQuery(id+"F21.wireOp",EDGE,"E151")])]});
            var Q2;
            Q2=makeQuery(id+"F20.opExtrude","SWEPT_EDGE",EDGE,{"disambiguationData":[OSD([sQuery(id+"F19.wireOp",EDGE,"E147.MirrorCS"),sQuery(id+"F19.wireOp",EDGE,"E148.MirrorCS")])]});
            var Q3;
            Q3=makeQuery(id+"F20.opExtrude","SWEPT_EDGE",EDGE,{"disambiguationData":[OSD([sQuery(id+"F19.wireOp",EDGE,"E143"),sQuery(id+"F19.wireOp",EDGE,"E144")])]});
            fillet(context, id + "F23", {"entities" : qUnion([Q0, Q1, Q2, Q3]), "radius" : 1.27 * mm, "tangentPropagation" : true, "allowEdgeOverflow" : false});
        }
        {
            var Q0;
            Q0=makeQuery(id+"F7.opExtrude","CAP_FACE",FACE,{"disambiguationData":[OSD([sQuery(id+"F4.wireOp",EDGE,"E34.MirrorCS"),sQuery(id+"F4.wireOp",EDGE,"E36.MirrorCS"),sQuery(id+"F4.wireOp",EDGE,"E38.MirrorCS"),sQuery(id+"F4.wireOp",EDGE,"E40.MirrorCS")])],"isStart":false});
            var sketch = newSketch(context, id + "F24", { "sketchPlane" : qUnion([Q0])});
            skLineSegment(sketch, "E156.bottom", {"start": v(-21.07, 38.33) * mm, "end": v(-6.85, 38.33) * mm});
            skLineSegment(sketch, "E156.top", {"start": v(-21.07, 20.53) * mm, "end": v(-6.85, 20.53) * mm});
            skLineSegment(sketch, "E156.left", {"start": v(-21.07, 38.33) * mm, "end": v(-21.07, 20.53) * mm});
            skLineSegment(sketch, "E156.right", {"start": v(-6.85, 38.33) * mm, "end": v(-6.85, 20.53) * mm});
            skSolve(sketch);
        }
        {
            var Q0;
            Q0 = qSketchRegion(id + "F24", true);
            extrude(context, id + "F25", {"entities" : qUnion([Q0]), "operationType" : NewBodyOperationType.REMOVE, "oppositeDirection" : true, "depth" : 2.54 * mm});
        }
    });
